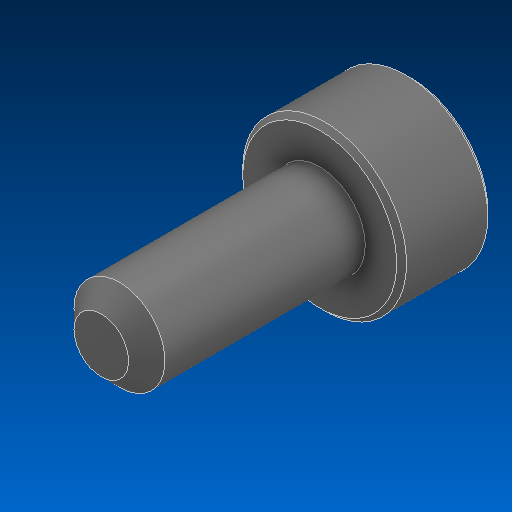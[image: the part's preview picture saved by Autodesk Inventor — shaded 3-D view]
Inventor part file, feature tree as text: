
AUTODESK INVENTOR PART (.ipt)
format: ipt  version: 2022.2 (Build 262287000, 287)  size: 135,168 bytes
history: native  units: in
note: dims shown in document units (in); Inventor stores cm internally (conversion verified against a paired STEP export)
features: chamfer x1
ambient origin geometry x8: Origin, YZ Plane, XZ Plane, XY Plane, X Axis, Y Axis, Z Axis, Center Point
bodies: Solid1 (feature_tree)
feature tree (1):
  chamfer  "Chamfer2"  [1 undecoded]
note: 1 required parameter value undecoded (feature->parameter linkage not recoverable at this tier; creation-order binding heuristic only, values carry confidence <= 0.55)
